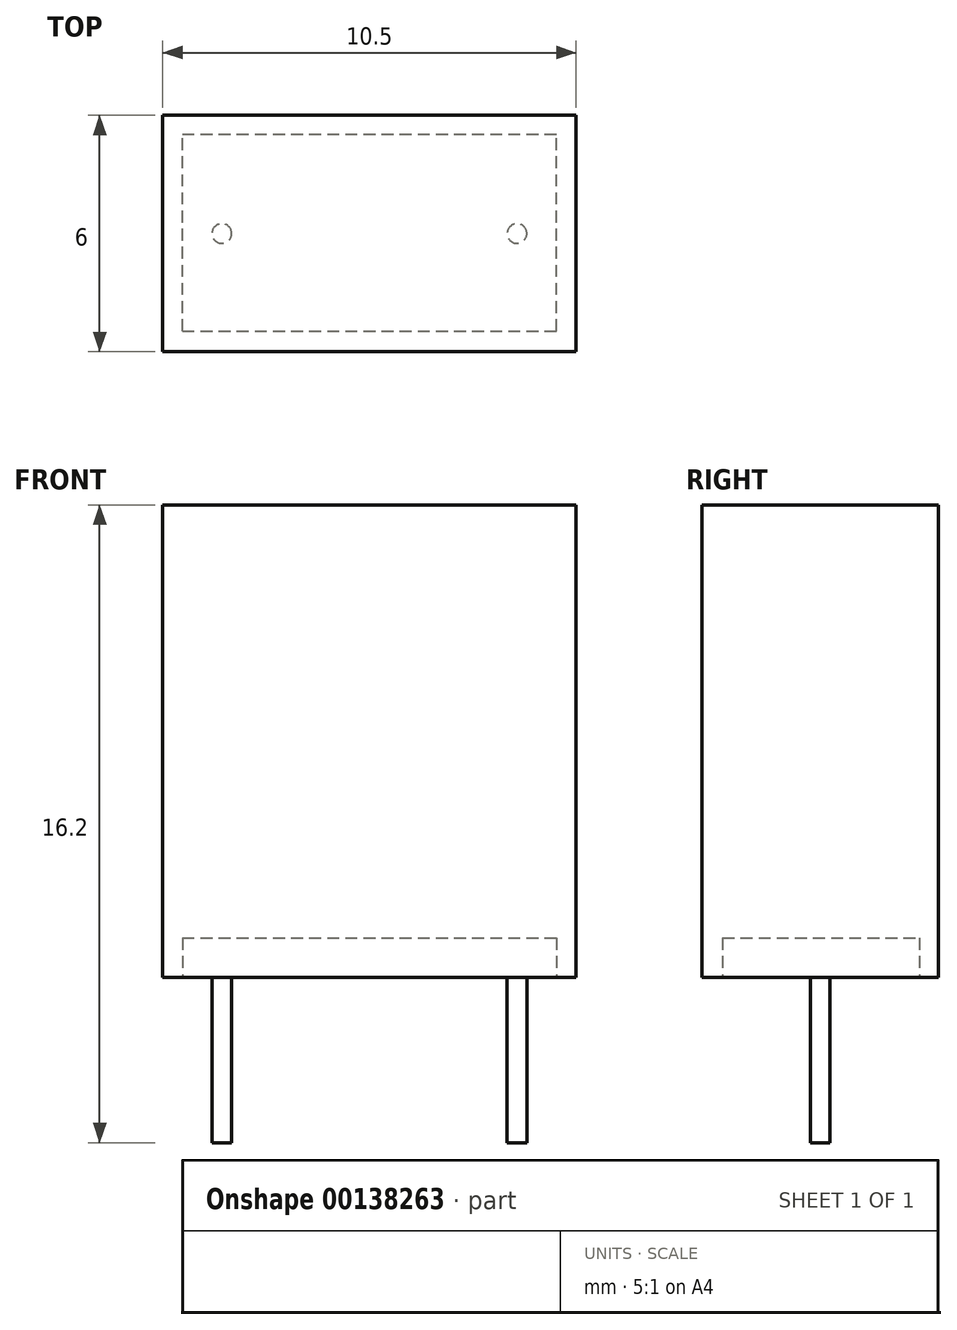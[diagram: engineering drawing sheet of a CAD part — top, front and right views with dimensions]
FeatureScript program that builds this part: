
annotation { "Feature Type Name" : "Feature", "Feature Type Description" : "" }
export const myFeature = defineFeature(function(context is Context, id is Id, definition is map)
    precondition{}
    {
        {
            var Q0;
            Q0=qCreatedBy(makeId("Front.planeOp"),FACE);
            var sketch = newSketch(context, id + "F0", { "sketchPlane" : qUnion([Q0])});
            skLineSegment(sketch, "E0.bottom", {"start": v(-5.25, 0) * mm, "end": v(5.25, 0) * mm});
            skLineSegment(sketch, "E0.top", {"start": v(-5.25, 12) * mm, "end": v(5.25, 12) * mm});
            skLineSegment(sketch, "E0.left", {"start": v(-5.25, 0) * mm, "end": v(-5.25, 12) * mm});
            skLineSegment(sketch, "E0.right", {"start": v(5.25, 0) * mm, "end": v(5.25, 12) * mm});
            skSolve(sketch);
        }
        {
            var Q0;
            Q0=makeQuery(id+"F0.imprint","IMPRINT",FACE,{"disambiguationData":[TD([[makeQuery(id+"F0.imprint","IMPRINT",EDGE,{"derivedFrom":sQuery(id+"F0.wireOp",EDGE,"E0.bottom")}),1.0]])]});
            extrude(context, id + "F1", {"entities" : qUnion([Q0]), "depth" : 3 * mm, "hasSecondDirection" : true, "secondDirectionOppositeDirection" : true, "secondDirectionDepth" : 3 * mm});
        }
        {
            var Q0;
            Q0=qCreatedBy(makeId("Top.planeOp"),FACE);
            var sketch = newSketch(context, id + "F2", { "sketchPlane" : qUnion([Q0])});
            skCircle(sketch, "E1", {"center": v(-3.75, 0) * mm, "radius": 0.25 * mm});
            skCircle(sketch, "E2.MirrorC", {"center": v(3.75, 0) * mm, "radius": 0.25 * mm});
            skSolve(sketch);
        }
        {
            var Q0;
            Q0 = qSketchRegion(id + "F2", true);
            extrude(context, id + "F3", {"entities" : qUnion([Q0]), "oppositeDirection" : true, "offsetDistance" : 25 * mm, "depth" : 4.2 * mm});
        }
        {
            var Q0;
            Q0=makeQuery(id+"F1.opExtrude","SWEPT_FACE",FACE,{"disambiguationData":[OSD([sQuery(id+"F0.wireOp",EDGE,"E0.bottom")])]});
            var sketch = newSketch(context, id + "F4", { "sketchPlane" : qUnion([Q0])});
            skLineSegment(sketch, "E3.bottom", {"start": v(-4.75, 2.48) * mm, "end": v(4.75, 2.48) * mm});
            skLineSegment(sketch, "E3.top", {"start": v(-4.75, -2.52) * mm, "end": v(4.75, -2.52) * mm});
            skLineSegment(sketch, "E3.left", {"start": v(-4.75, 2.48) * mm, "end": v(-4.75, -2.52) * mm});
            skLineSegment(sketch, "E3.right", {"start": v(4.75, 2.48) * mm, "end": v(4.75, -2.52) * mm});
            skSolve(sketch);
        }
        {
            var Q0;
            Q0=makeQuery(id+"F4.imprint","IMPRINT",FACE,{"disambiguationData":[TD([[makeQuery(id+"F4.imprint","IMPRINT",EDGE,{"derivedFrom":sQuery(id+"F4.wireOp",EDGE,"E3.bottom")}),-1.0]])]});
            extrude(context, id + "F5", {"entities" : qUnion([Q0]), "oppositeDirection" : true, "depth" : 1 * mm, "offsetDistance" : 25 * mm});
        }
        {
            var Q0;
            Q0=makeQuery(id+"F5.opExtrude","SWEPT_BODY",BODY,{"disambiguationData":[OSD([sQuery(id+"F4.wireOp",EDGE,"E3.bottom"),sQuery(id+"F4.wireOp",EDGE,"E3.top"),sQuery(id+"F4.wireOp",EDGE,"E3.left"),sQuery(id+"F4.wireOp",EDGE,"E3.right")])]});
            var Q1;
            Q1=makeQuery(id+"F1.opExtrude","SWEPT_BODY",BODY,{"disambiguationData":[OSD([sQuery(id+"F0.wireOp",EDGE,"E0.bottom"),sQuery(id+"F0.wireOp",EDGE,"E0.top"),sQuery(id+"F0.wireOp",EDGE,"E0.left"),sQuery(id+"F0.wireOp",EDGE,"E0.right")])]});
            booleanBodies(context, id + "F6", {"operationType" : BooleanOperationType.SUBTRACTION, "tools" : qUnion([Q0]), "targets" : qUnion([Q1]), "keepTools" : true});
        }
    });
